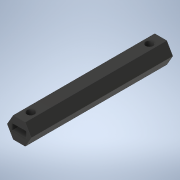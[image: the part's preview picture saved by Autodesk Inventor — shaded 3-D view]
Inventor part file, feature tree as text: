
AUTODESK INVENTOR PART (.ipt)
format: ipt  version: 2020 (Build 240168000, 168)  size: 207,872 bytes
history: native  units: mm
features: extrude x9, sketch x9, projected_geometry x4, mirror x2, plane x1
ambient origin geometry x8: Origin, YZ Plane, XZ Plane, XY Plane, X Axis, Y Axis, Z Axis, Center Point
bodies: Solid1 (feature_tree)
feature tree (25):
  extrude  "Extrusion1"  Depth=55.8mm TaperAngle=0.0deg
  extrude  "Extrusion2"  Depth=5.6mm
  extrude  "Extrusion3"  Depth=3.0mm
  plane  "Work Plane1"
  mirror  "Mirror1"
  extrude  "Extrusion4"  TaperAngle=0.0deg  [1 undecoded]
  extrude  "Extrusion5"  TaperAngle=120.0deg  [1 undecoded]
  extrude  "Extrusion6"  Depth=9.5mm TaperAngle=0.0deg
  extrude  "Extrusion8"  Depth=5.6mm
  extrude  "Extrusion9"  Depth=6.0mm TaperAngle=0.0deg
  extrude  "Extrusion10"  TaperAngle=120.0deg  [1 undecoded]
  mirror  "Mirror3"
  sketch  "Sketch1"  dims[d0=4.1mm d1=55.8mm d2=0.0mm]
  sketch  "Sketch2"  dims[d3=2.5mm d4=5.6mm]
  sketch  "Sketch3"  dims[d5=6.0mm d6=0.0mm d7=3.0mm]
  sketch  "Sketch4"  dims[d8=9.5mm d9=0.0mm d10=0.0mm]
  sketch  "Sketch5"  dims[d11=6.0mm d12=120.0deg]
  projected_geometry  "Projected Loop1"
  projected_geometry  "Projected Loop2"
  sketch  "Sketch6"  dims[d13=120.0deg d14=9.5mm d15=0.0mm]
  sketch  "Sketch8"  dims[d16=2.5mm d17=5.6mm]
  sketch  "Sketch9"  dims[d18=6.0mm d19=6.0mm d20=0.0mm]
  projected_geometry  "Projected Loop4"
  sketch  "Sketch10"  dims[d21=120.0deg d22=120.0deg d23=6.0mm d24=0.0mm d25=1.9345mm d32=5.6mm d33=2.5mm d34=6.5mm d35=0.0mm d36=90.0deg d37=3.0mm d38=0.0mm d39=4.5mm d40=8.0mm d41=0.0mm d42=30.0deg d43=150.0deg d44=2.5mm d45=0.0mm d46=1.25mm d47=2.8mm]
  projected_geometry  "Projected Loop5"
note: 3 required parameter values undecoded (feature->parameter linkage not recoverable at this tier; creation-order binding heuristic only, values carry confidence <= 0.55)
